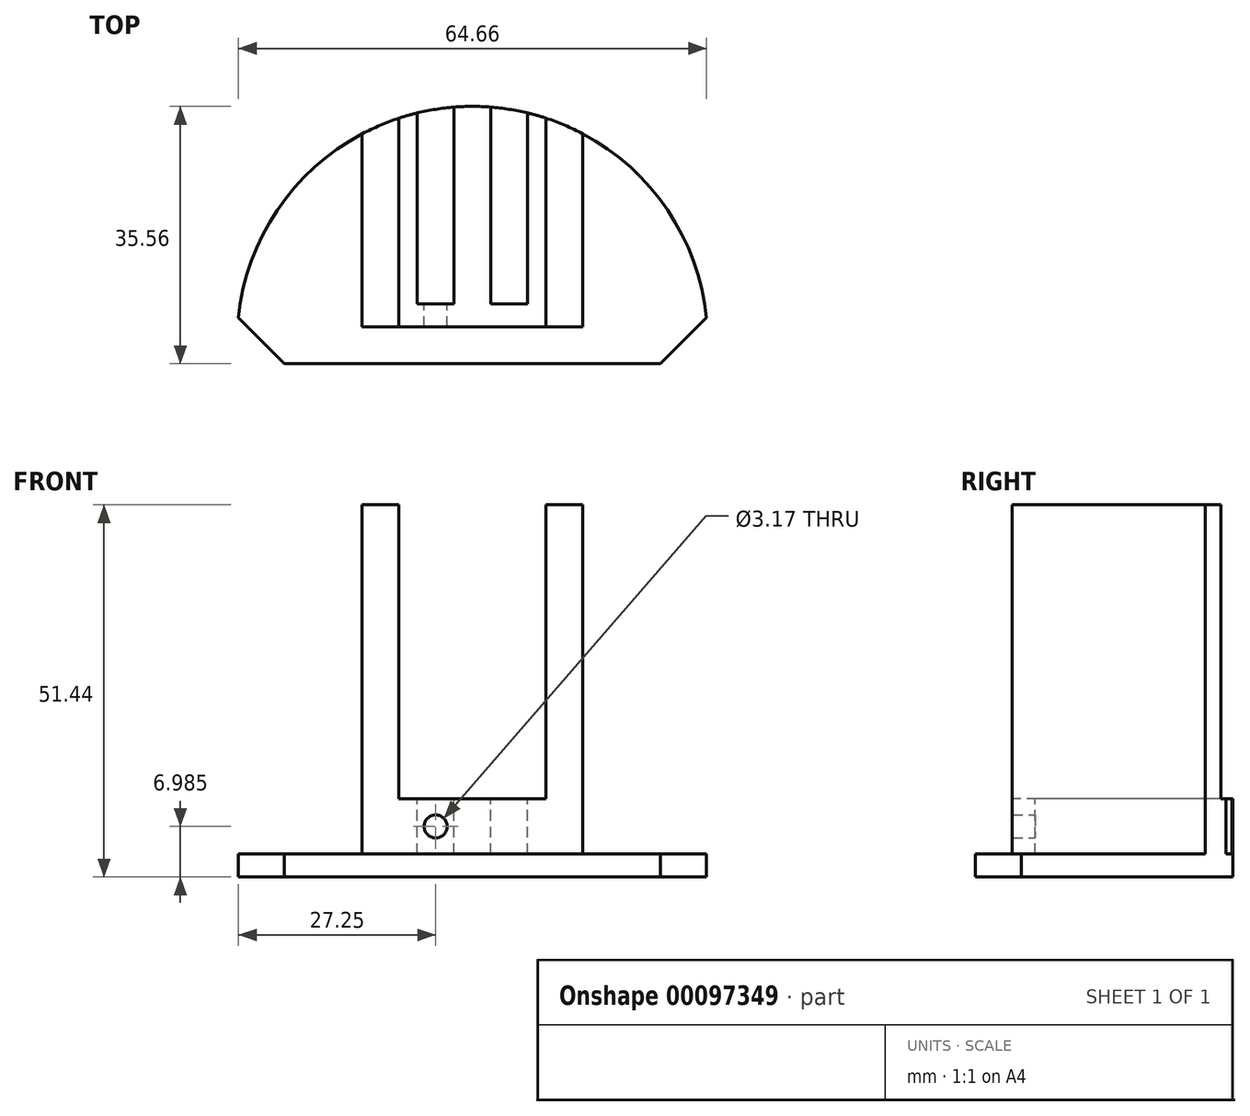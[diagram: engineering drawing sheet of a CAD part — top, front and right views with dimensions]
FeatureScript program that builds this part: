
annotation { "Feature Type Name" : "Feature", "Feature Type Description" : "" }
export const myFeature = defineFeature(function(context is Context, id is Id, definition is map)
    precondition{}
    {
        {
            var Q0;
            Q0=qCreatedBy(makeId("Top.planeOp"),FACE);
            var sketch = newSketch(context, id + "F0", { "sketchPlane" : qUnion([Q0])});
            skArc(sketch, "E0", {"start": v(32.33, 3.3) * mm, "mid": v(0, 32.5) * mm, "end": v(-32.33, 3.3) * mm});
            skLineSegment(sketch, "E1", {"start": v(0, 0) * mm, "end": v(0, 57.02) * mm, "construction": true});
            skPoint(sketch, "E2", {"position": v(0, 32.5) * mm});
            skLineSegment(sketch, "E3", {"start": v(-32.33, 3.3) * mm, "end": v(-25.98, -3.06) * mm});
            skLineSegment(sketch, "E4", {"start": v(-25.98, -3.06) * mm, "end": v(0, -3.06) * mm});
            skLineSegment(sketch, "E5.MirrorCS", {"start": v(25.98, -3.06) * mm, "end": v(0, -3.06) * mm});
            skLineSegment(sketch, "E6.MirrorCS", {"start": v(32.33, 3.3) * mm, "end": v(25.98, -3.06) * mm});
            skSolve(sketch);
        }
        {
            var Q0;
            Q0=makeQuery(id+"F0.imprint","IMPRINT",FACE,{"disambiguationData":[TD([[makeQuery(id+"F0.imprint","IMPRINT",EDGE,{"derivedFrom":sQuery(id+"F0.wireOp",EDGE,"E0")}),1.0]])]});
            extrude(context, id + "F1", {"entities" : qUnion([Q0]), "depth" : 3.17 * mm});
        }
        {
            var Q0;
            Q0=makeQuery(id+"F1.opExtrude","CAP_FACE",FACE,{"disambiguationData":[OSD([sQuery(id+"F0.wireOp",EDGE,"E0"),sQuery(id+"F0.wireOp",EDGE,"E3"),sQuery(id+"F0.wireOp",EDGE,"E4"),sQuery(id+"F0.wireOp",EDGE,"E5.MirrorCS"),sQuery(id+"F0.wireOp",EDGE,"E6.MirrorCS")])],"isStart":false});
            var sketch = newSketch(context, id + "F2", { "sketchPlane" : qUnion([Q0])});
            skLineSegment(sketch, "E7", {"start": v(0, 0) * mm, "end": v(0, 37.11) * mm, "construction": true});
            skLineSegment(sketch, "E8", {"start": v(15.24, 28.7) * mm, "end": v(15.24, 2.02) * mm});
            skLineSegment(sketch, "E9.MirrorCS", {"start": v(-15.24, 28.7) * mm, "end": v(-15.24, 2.02) * mm});
            skLineSegment(sketch, "E10", {"start": v(15.24, 2.02) * mm, "end": v(-15.24, 2.02) * mm});
            skPoint(sketch, "E11", {"position": v(0, 32.5) * mm});
            skSolve(sketch);
        }
        {
            var Q0;
            {var subQ0=sQuery(id+"F2.wireOp",EDGE,"E8");Q0=makeQuery(id+"F2.imprint","IMPRINT",FACE,{"disambiguationData":[TD([[makeQuery(id+"F2.imprint","IMPRINT",EDGE,{"derivedFrom":subQ0}),-1.0]])]});}
            extrude(context, id + "F3", {"entities" : qUnion([Q0]), "operationType" : NewBodyOperationType.ADD, "depth" : 7.62 * mm});
        }
        {
            var Q0;
            Q0=makeQuery(id+"F3.opExtrude","CAP_FACE",FACE,{"disambiguationData":[OSD([sQuery(id+"F0.wireOp",EDGE,"E0"),sQuery(id+"F2.wireOp",EDGE,"E8"),sQuery(id+"F2.wireOp",EDGE,"E9.MirrorCS"),sQuery(id+"F2.wireOp",EDGE,"E10")])],"isStart":false});
            var sketch = newSketch(context, id + "F4", { "sketchPlane" : qUnion([Q0])});
            skLineSegment(sketch, "E12", {"start": v(0, 32.5) * mm, "end": v(0, 2.02) * mm, "construction": true});
            skLineSegment(sketch, "E13", {"start": v(2.54, 32.4) * mm, "end": v(2.54, 5.2) * mm});
            skLineSegment(sketch, "E14.MirrorCS", {"start": v(-2.54, 32.4) * mm, "end": v(-2.54, 5.2) * mm});
            skLineSegment(sketch, "E15", {"start": v(7.62, 31.6) * mm, "end": v(7.62, 5.2) * mm});
            skLineSegment(sketch, "E16.MirrorCS", {"start": v(-7.62, 31.6) * mm, "end": v(-7.62, 5.2) * mm});
            skLineSegment(sketch, "E17", {"start": v(7.62, 5.2) * mm, "end": v(2.54, 5.2) * mm});
            skPoint(sketch, "E18.orphan", {"position": v(7.62, 2.02) * mm});
            skPoint(sketch, "E19.orphan", {"position": v(2.54, 2.02) * mm});
            skPoint(sketch, "E20.orphan", {"position": v(-2.54, 2.02) * mm});
            skPoint(sketch, "E21.orphan", {"position": v(-7.62, 2.02) * mm});
            skLineSegment(sketch, "E22.trimOffspring", {"start": v(-2.54, 5.2) * mm, "end": v(-7.62, 5.2) * mm});
            skSolve(sketch);
        }
        {
            var Q0;
            {var subQ0=sQuery(id+"F4.wireOp",EDGE,"E13");Q0=makeQuery(id+"F4.imprint","IMPRINT",FACE,{"disambiguationData":[TD([[makeQuery(id+"F4.imprint","IMPRINT",EDGE,{"derivedFrom":subQ0}),1.0]])]});}
            var Q1;
            {var subQ0=sQuery(id+"F4.wireOp",EDGE,"E14.MirrorCS");Q1=makeQuery(id+"F4.imprint","IMPRINT",FACE,{"disambiguationData":[TD([[makeQuery(id+"F4.imprint","IMPRINT",EDGE,{"derivedFrom":subQ0}),-1.0]])]});}
            extrude(context, id + "F5", {"entities" : qUnion([Q0, Q1]), "operationType" : NewBodyOperationType.REMOVE, "oppositeDirection" : true, "depth" : 7.62 * mm});
        }
        {
            var Q0;
            Q0=makeQuery(id+"F3.opExtrude","CAP_FACE",FACE,{"disambiguationData":[OSD([sQuery(id+"F0.wireOp",EDGE,"E0"),sQuery(id+"F2.wireOp",EDGE,"E8"),sQuery(id+"F2.wireOp",EDGE,"E9.MirrorCS"),sQuery(id+"F2.wireOp",EDGE,"E10")])],"isStart":false});
            var sketch = newSketch(context, id + "F6", { "sketchPlane" : qUnion([Q0])});
            skLineSegment(sketch, "E23", {"start": v(0, 2.02) * mm, "end": v(0, 32.5) * mm, "construction": true});
            skLineSegment(sketch, "E24", {"start": v(-10.16, 30.87) * mm, "end": v(-10.16, 2.02) * mm});
            skLineSegment(sketch, "E25.MirrorCS", {"start": v(10.16, 30.87) * mm, "end": v(10.16, 2.02) * mm});
            skSolve(sketch);
        }
        {
            var Q0;
            {var subQ0=sQuery(id+"F6.wireOp",EDGE,"E24");Q0=makeQuery(id+"F6.imprint","IMPRINT",FACE,{"disambiguationData":[TD([[makeQuery(id+"F6.imprint","IMPRINT",EDGE,{"derivedFrom":subQ0}),-1.0]])]});}
            var Q1;
            {var subQ0=sQuery(id+"F6.wireOp",EDGE,"E25.MirrorCS");Q1=makeQuery(id+"F6.imprint","IMPRINT",FACE,{"disambiguationData":[TD([[makeQuery(id+"F6.imprint","IMPRINT",EDGE,{"derivedFrom":subQ0}),1.0]])]});}
            extrude(context, id + "F7", {"entities" : qUnion([Q0, Q1]), "operationType" : NewBodyOperationType.ADD, "depth" : 40.64 * mm});
        }
        {
            var Q0;
            Q0=makeQuery(id+"F5.boolean.opBoolean","COPY",FACE,{"derivedFrom":makeQuery(id+"F5.opExtrude","SWEPT_FACE",FACE,{"disambiguationData":[OSD([sQuery(id+"F4.wireOp",EDGE,"E22.trimOffspring")])]})});
            var sketch = newSketch(context, id + "F8", { "sketchPlane" : qUnion([Q0])});
            skLineSegment(sketch, "E26", {"start": v(7.62, 6.99) * mm, "end": v(-7.7, 6.99) * mm, "construction": true});
            skLineSegment(sketch, "E27", {"start": v(5.08, 3.18) * mm, "end": v(5.08, 10.8) * mm, "construction": true});
            skCircle(sketch, "E28", {"center": v(5.08, 6.99) * mm, "radius": 1.59 * mm});
            skLineSegment(sketch, "E29", {"start": v(0, 0) * mm, "end": v(0, 26.67) * mm, "construction": true});
            skCircle(sketch, "E30.MirrorC", {"center": v(-5.08, 6.99) * mm, "radius": 1.59 * mm});
            skSolve(sketch);
        }
        {
            var Q0;
            Q0=makeQuery(id+"F8.imprint","IMPRINT",FACE,{"disambiguationData":[TD([[makeQuery(id+"F8.imprint","IMPRINT",EDGE,{"derivedFrom":sQuery(id+"F8.wireOp",EDGE,"E30.MirrorC")}),-1.0]])]});
            var Q1;
            Q1=makeQuery(id+"F8.imprint","IMPRINT",FACE,{"disambiguationData":[TD([[makeQuery(id+"F8.imprint","IMPRINT",EDGE,{"derivedFrom":sQuery(id+"F8.wireOp",EDGE,"E28")}),1.0]])]});
            extrude(context, id + "F9", {"entities" : qUnion([Q0, Q1]), "operationType" : NewBodyOperationType.REMOVE, "oppositeDirection" : true, "depth" : 25.4 * mm});
        }
        {
            var Q0;
            Q0=makeQuery(id+"F8.imprint","IMPRINT",FACE,{"disambiguationData":[TD([[makeQuery(id+"F8.imprint","IMPRINT",EDGE,{"derivedFrom":sQuery(id+"F8.wireOp",EDGE,"E28")}),1.0]])]});
            extrude(context, id + "F10", {"entities" : qUnion([Q0]), "operationType" : NewBodyOperationType.REMOVE, "oppositeDirection" : true, "depth" : 25.4 * mm});
        }
    });
